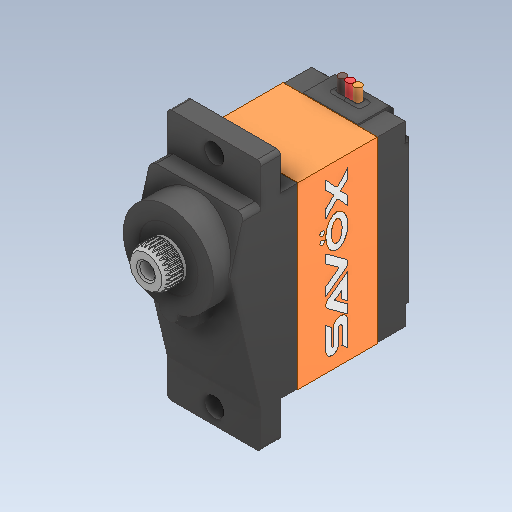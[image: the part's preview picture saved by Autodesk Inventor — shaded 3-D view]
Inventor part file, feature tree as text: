
AUTODESK INVENTOR PART (.ipt)
format: ipt  version: 2020.3 (Build 243373000, 373)  size: 912,384 bytes
history: native  units: mm
features: other x13, shell x1
ambient origin geometry x8: Origin, YZ Plane, XZ Plane, XY Plane, X Axis, Y Axis, Z Axis, Center Point
bodies: Solid1 (feature_tree), Solid2 (feature_tree), Solid3 (feature_tree), Solid4 (feature_tree), Solid5 (feature_tree), Solid6 (feature_tree), Solid7 (feature_tree), Solid8 (feature_tree), Solid9 (feature_tree), Solid10 (feature_tree), Solid11 (feature_tree), Solid12 (feature_tree), Solid13 (feature_tree), Solid14 (feature_tree)
feature tree (14):
  other  "brep_12"
  other  "brep_5"
  other  "brep_11"
  other  "brep_10"
  other  "brep_9"
  other  "brep_8"
  other  "brep_7"
  other  "brep_6"
  shell  "shell_1"  [1 undecoded]
  other  "brep_13"
  other  "brep_4"
  other  "brep_3"
  other  "brep_2"
  other  "brep_1"
note: 1 required parameter value undecoded (feature->parameter linkage not recoverable at this tier; creation-order binding heuristic only, values carry confidence <= 0.55)
